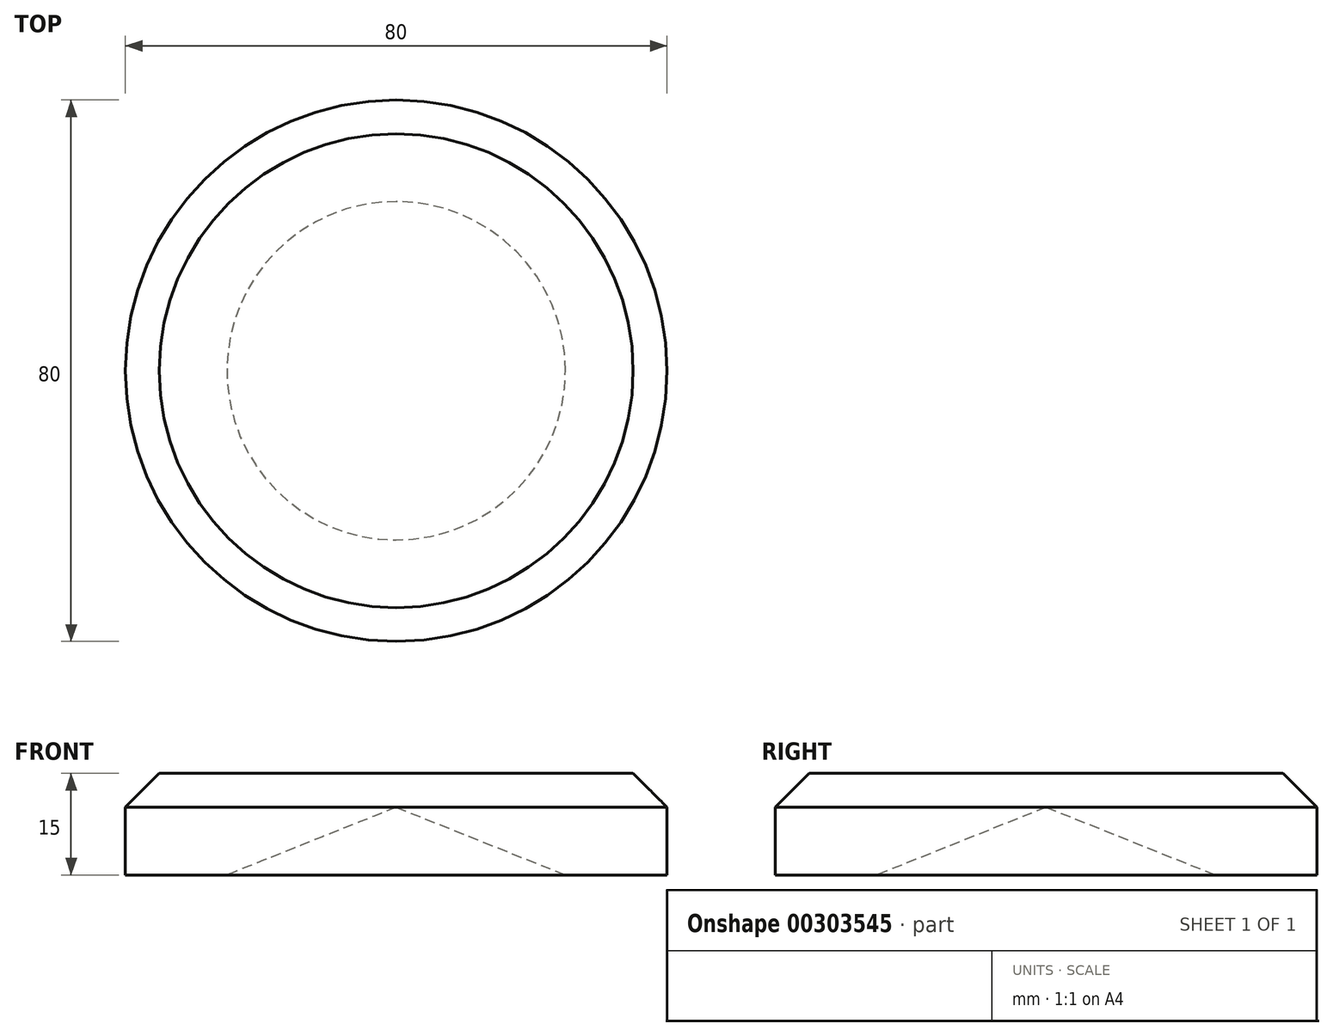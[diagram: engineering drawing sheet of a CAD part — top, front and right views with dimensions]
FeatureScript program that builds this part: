
annotation { "Feature Type Name" : "Feature", "Feature Type Description" : "" }
export const myFeature = defineFeature(function(context is Context, id is Id, definition is map)
    precondition{}
    {
        {
            var Q0;
            Q0=qCreatedBy(makeId("Top.planeOp"),FACE);
            var sketch = newSketch(context, id + "F0", { "sketchPlane" : qUnion([Q0])});
            skCircle(sketch, "E0", {"center": v(0, 0) * mm, "radius": 40 * mm});
            skSolve(sketch);
        }
        {
            var Q0;
            Q0=makeQuery(id+"F0.imprint","IMPRINT",FACE,{"disambiguationData":[TD([[makeQuery(id+"F0.imprint","IMPRINT",EDGE,{"derivedFrom":sQuery(id+"F0.wireOp",EDGE,"E0")}),1.0]])]});
            extrude(context, id + "F1", {"entities" : qUnion([Q0]), "depth" : 15 * mm});
        }
        {
            var Q0;
            Q0=makeQuery(id+"F1.opExtrude","CAP_EDGE",EDGE,{"disambiguationData":[OSD([sQuery(id+"F0.wireOp",EDGE,"E0")])],"isStart":false});
            chamfer(context, id + "F2", {"entities" : qUnion([Q0]), "width" : 5 * mm, "tangentPropagation" : true});
        }
        {
            var Q0;
            Q0=makeQuery(id+"F1.opExtrude","CAP_FACE",FACE,{"disambiguationData":[OSD([sQuery(id+"F0.wireOp",EDGE,"E0")])],"isStart":true});
            var sketch = newSketch(context, id + "F3", { "sketchPlane" : qUnion([Q0])});
            skCircle(sketch, "E1", {"center": v(0, 0) * mm, "radius": 25 * mm});
            skSolve(sketch);
        }
        {
            var Q0;
            Q0=makeQuery(id+"F3.imprint","IMPRINT",FACE,{"disambiguationData":[TD([[makeQuery(id+"F3.imprint","IMPRINT",EDGE,{"derivedFrom":sQuery(id+"F3.wireOp",EDGE,"E1")}),1.0]])]});
            extrude(context, id + "F4", {"entities" : qUnion([Q0]), "operationType" : NewBodyOperationType.REMOVE, "oppositeDirection" : true, "depth" : 10 * mm});
        }
        {
            var Q0;
            Q0=makeQuery(id+"F4.boolean.opBoolean","COPY",EDGE,{"derivedFrom":makeQuery(id+"F4.opExtrude","CAP_EDGE",EDGE,{"disambiguationData":[OSD([sQuery(id+"F3.wireOp",EDGE,"E1")])],"isStart":false})});
            chamfer(context, id + "F5", {"entities" : qUnion([Q0]), "chamferType" : ChamferType.TWO_OFFSETS, "width1" : 25 * mm, "oppositeDirection" : false, "width2" : 10 * mm, "tangentPropagation" : true});
        }
    });
